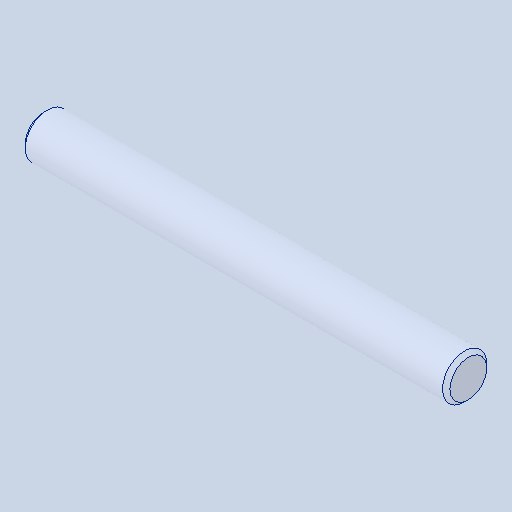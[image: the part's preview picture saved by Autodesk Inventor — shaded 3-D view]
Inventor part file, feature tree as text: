
AUTODESK INVENTOR PART (.ipt)
format: ipt  version: 2023.4 (Build 274418000, 418)  size: 86,016 bytes
history: native  units: in
note: dims shown in document units (in); Inventor stores cm internally (conversion verified against a paired STEP export)
features: chamfer x1
ambient origin geometry x8: Origin, YZ Plane, XZ Plane, XY Plane, X Axis, Y Axis, Z Axis, Center Point
bodies: Solid1 (feature_tree)
feature tree (1):
  chamfer  "Chamfer1"  [1 undecoded]
note: 1 required parameter value undecoded (feature->parameter linkage not recoverable at this tier; creation-order binding heuristic only, values carry confidence <= 0.55)
